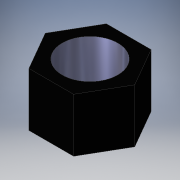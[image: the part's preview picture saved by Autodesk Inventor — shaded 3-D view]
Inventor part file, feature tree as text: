
AUTODESK INVENTOR PART (.ipt)
format: ipt  version: 2016 (Build 200138000, 138)  size: 102,912 bytes
history: native  units: in
note: dims shown in document units (in); Inventor stores cm internally (conversion verified against a paired STEP export)
features: extrude x1, sketch x1
ambient origin geometry x8: Origin, YZ Plane, XZ Plane, XY Plane, X Axis, Y Axis, Z Axis, Center Point
bodies: Solid1 (feature_tree)
feature tree (2):
  extrude  "Extrusion1"  Depth=0.0984in
  sketch  "Sketch1"  dims[d0=0.122in d1=0.0984in d2=0.1181in d3=0.0in]
